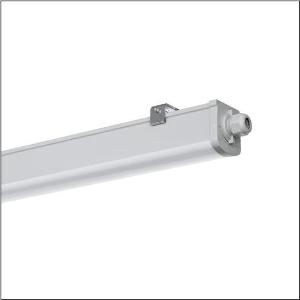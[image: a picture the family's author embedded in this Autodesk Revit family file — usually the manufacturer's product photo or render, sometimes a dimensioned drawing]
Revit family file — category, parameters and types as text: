
# Revit family: monsun_r__31_51fa207p430b_b845
name_source: partatom
category: Lighting Fixtures
units: mm (PartAtom-declared; Revit-internal decimal feet)

## family parameters
Cut with Voids When Loaded = No
Host = Face
Light Source = No
Part Type = Normal
Room Calculation Point = No
Round Connector Dimension = Use Diameter
Shared = No

## types (1)
- Monsun® 31 (1 x LED, 3800 lm, 28 W, 4000K)
    Apparent Load = 28 VA
    CIE Flux Codes = 42 72 91 92 100
    Color Rendering = 80
    Color Temperature = 4000K
    Default Elevation = 1800 mm
    Description = Monsun® 31, damp-proof luminaire, primary optical cover: diffuser, of PC, frosted, light emission: direct distribution, primary light characteristic: symmetric, installation type: surface-mounted, LED, rated luminous flux: 3.800lm, luminous efficacy: 136lm/W, light colour: 840, colour temperature: 4000K, control gear: ECG, with terminal, 3+1-pole, max. 2.5mm², through-wiring: 3x 2.5mm² + 1x 1.5mm², mains connection: 220..240V, AC, 50/60Hz, rated input power: 28W, housing, luminaire housing, of PC, light grey (RAL 7035), length: 1.458mm, width: 68mm, height: 76mm, protection rating (complete): IP66, insulation class (complete): insulation class II (safety insulation), certification: CE, ENEC, UKCA, protection symbol: D, impact resistance: IK08, permissible operating ambient temperature: -20..+40°C, corresponds to IFS (International Featured Standards) requirements for safety and quality in the food industry, contact your sales advisor before using the luminaires in applications with unclear chemical exposure, large temperature fluctuations or condensation-forming humidity, packaging unit: 1 piece
    Height = 77 mm
    Lamp = 1 x LED
    Lamp Light Flux = 3800 lm
    Lamp Power = 28 W
    Lamp count = 1
    Length = 1518 mm
    Luminous efficacy = 136 lm/W
    Manufacturer = Siteco
    ModVariant = No
    Model = 51FA207P430B
    Mounting Place = Ceiling
    Mounting Type = Surface mounted
    Number of Poles = 1
    OnlyDefault = Yes
    Power Factor = 1
    Product Name = Monsun® 31
    Product group = damp-proof luminaire
    ProductGroupID = 300
    Protection Class = Protection class II
    Protection Degree = IP 66
    RLX_Detail_Level = 1
    RLX_Emergency_Light_Flux = 0 lm
    RLX_Emergency_Type = 0
    RLX_Emergency_Type_DB = No
    RlxData = <blob elided: 33201 chars, md5=582fcd7c>
    Socket = socket
    Standby Power = 0 W
    System Light Flux = 3800 lm
    System Power = 28 W
    Type Comments = Product without accessories
    Type Image = l_1006174.jpg
    URL = http://relux.com
    VarID = ---
    Voltage = 0 V
    Weight = 0.00 kg
    Width = 69 mm

## geometry (parser evidence)
native form markers: Blend x4, Sweep x12
no freeform markers — native parametric forms only
